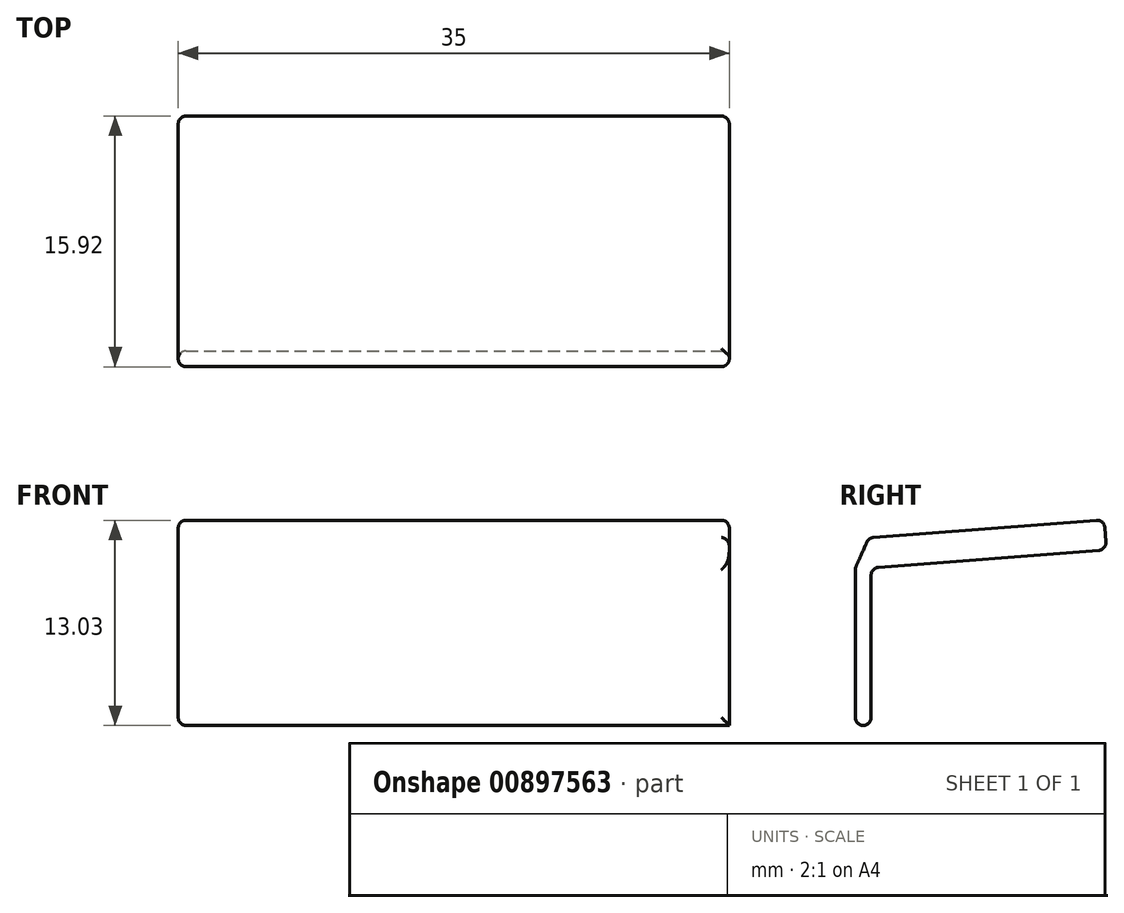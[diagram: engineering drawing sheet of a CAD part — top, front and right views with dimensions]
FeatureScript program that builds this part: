
annotation { "Feature Type Name" : "Feature", "Feature Type Description" : "" }
export const myFeature = defineFeature(function(context is Context, id is Id, definition is map)
    precondition{}
    {
        {
            var Q0;
            Q0=qCreatedBy(makeId("Top.planeOp"),FACE);
            var sketch = newSketch(context, id + "F0", { "sketchPlane" : qUnion([Q0])});
            skLineSegment(sketch, "E0.bottom", {"start": v(-40.78, 27.46) * mm, "end": v(-5.78, 27.46) * mm});
            skLineSegment(sketch, "E0.top", {"start": v(-40.78, 26.46) * mm, "end": v(-5.78, 26.46) * mm});
            skLineSegment(sketch, "E0.left", {"start": v(-40.78, 27.46) * mm, "end": v(-40.78, 26.46) * mm});
            skLineSegment(sketch, "E0.right", {"start": v(-5.78, 27.46) * mm, "end": v(-5.78, 26.46) * mm});
            skSolve(sketch);
        }
        {
            var Q0;
            Q0 = qSketchRegion(id + "F0", true);
            extrude(context, id + "F1", {"entities" : qUnion([Q0]), "depth" : 10 * mm, "offsetDistance" : 25 * mm});
        }
        {
            var Q0;
            Q0=makeQuery(id+"F1.opExtrude","SWEPT_FACE",FACE,{"disambiguationData":[OSD([sQuery(id+"F0.wireOp",EDGE,"E0.left")])]});
            var sketch = newSketch(context, id + "F2", { "sketchPlane" : qUnion([Q0])});
            skLineSegment(sketch, "E1", {"start": v(-26.46, 10) * mm, "end": v(-27.46, 10) * mm});
            skLineSegment(sketch, "E2", {"start": v(-27.46, 10) * mm, "end": v(-27.32, 11.91) * mm});
            skLineSegment(sketch, "E3", {"start": v(-27.32, 11.91) * mm, "end": v(-26.46, 10) * mm});
            skSolve(sketch);
        }
        {
            var Q0;
            Q0 = qSketchRegion(id + "F2", true);
            extrude(context, id + "F3", {"entities" : qUnion([Q0]), "operationType" : NewBodyOperationType.ADD, "oppositeDirection" : true, "depth" : 35 * mm, "offsetDistance" : 25 * mm});
        }
        {
            var Q0;
            Q0=makeQuery(id+"F3.opExtrude","SWEPT_FACE",FACE,{"disambiguationData":[OSD([sQuery(id+"F2.wireOp",EDGE,"E2")])]});
            var sketch = newSketch(context, id + "F4", { "sketchPlane" : qUnion([Q0])});
            skLineSegment(sketch, "E4.bottom", {"start": v(5.78, 7.86) * mm, "end": v(40.78, 7.86) * mm});
            skLineSegment(sketch, "E4.top", {"start": v(5.78, 9.77) * mm, "end": v(40.78, 9.77) * mm});
            skLineSegment(sketch, "E4.left", {"start": v(5.78, 7.86) * mm, "end": v(5.78, 9.77) * mm});
            skLineSegment(sketch, "E4.right", {"start": v(40.78, 7.86) * mm, "end": v(40.78, 9.77) * mm});
            skSolve(sketch);
        }
        {
            var Q0;
            Q0 = qSketchRegion(id + "F4", true);
            extrude(context, id + "F5", {"entities" : qUnion([Q0]), "operationType" : NewBodyOperationType.ADD, "depth" : 15 * mm, "offsetDistance" : 25 * mm});
        }
        {
            var Q0;
            Q0=makeQuery(id+"F1.opExtrude","SWEPT_FACE",FACE,{"disambiguationData":[OSD([sQuery(id+"F0.wireOp",EDGE,"E0.top")])]});
            var Q1;
            Q1=makeQuery(id+"F5.boolean.opBoolean","MERGE",FACE,{"derivedFrom":[makeQuery(id+"F3.boolean.opBoolean","MERGE",FACE,{"derivedFrom":[makeQuery(id+"F1.opExtrude","SWEPT_FACE",FACE,{"disambiguationData":[OSD([sQuery(id+"F0.wireOp",EDGE,"E0.left")])]}),makeQuery(id+"F3.opExtrude","CAP_FACE",FACE,{"disambiguationData":[OSD([sQuery(id+"F2.wireOp",EDGE,"E1"),sQuery(id+"F2.wireOp",EDGE,"E2"),sQuery(id+"F2.wireOp",EDGE,"E3")])],"isStart":true})]}),makeQuery(id+"F5.opExtrude","SWEPT_FACE",FACE,{"disambiguationData":[OSD([sQuery(id+"F4.wireOp",EDGE,"E4.right")])]})]});
            var Q2;
            Q2=makeQuery(id+"F5.opExtrude","SWEPT_FACE",FACE,{"disambiguationData":[OSD([sQuery(id+"F4.wireOp",EDGE,"E4.bottom")])]});
            var Q3;
            Q3=makeQuery(id+"F1.opExtrude","SWEPT_FACE",FACE,{"disambiguationData":[OSD([sQuery(id+"F0.wireOp",EDGE,"E0.bottom")])]});
            var Q4;
            Q4=makeQuery(id+"F5.opExtrude","CAP_FACE",FACE,{"disambiguationData":[OSD([sQuery(id+"F4.wireOp",EDGE,"E4.bottom"),sQuery(id+"F4.wireOp",EDGE,"E4.top"),sQuery(id+"F4.wireOp",EDGE,"E4.left"),sQuery(id+"F4.wireOp",EDGE,"E4.right")])],"isStart":false});
            var Q5;
            Q5=makeQuery(id+"F5.opExtrude","SWEPT_FACE",FACE,{"disambiguationData":[OSD([sQuery(id+"F4.wireOp",EDGE,"E4.top")])]});
            var Q6;
            Q6=makeQuery(id+"F3.boolean.opBoolean","MERGE",FACE,{"derivedFrom":[makeQuery(id+"F1.opExtrude","CAP_FACE",FACE,{"disambiguationData":[OSD([sQuery(id+"F0.wireOp",EDGE,"E0.bottom"),sQuery(id+"F0.wireOp",EDGE,"E0.top"),sQuery(id+"F0.wireOp",EDGE,"E0.left"),sQuery(id+"F0.wireOp",EDGE,"E0.right")])],"isStart":false}),makeQuery(id+"F3.opExtrude","SWEPT_FACE",FACE,{"disambiguationData":[OSD([sQuery(id+"F2.wireOp",EDGE,"E3")])]})]});
            fillet(context, id + "F6", {"entities" : qUnion([Q0, Q1, Q2, Q3, Q4, Q5, Q6]), "radius" : 0.5 * mm, "tangentPropagation" : true, "allowEdgeOverflow" : false});
        }
    });
